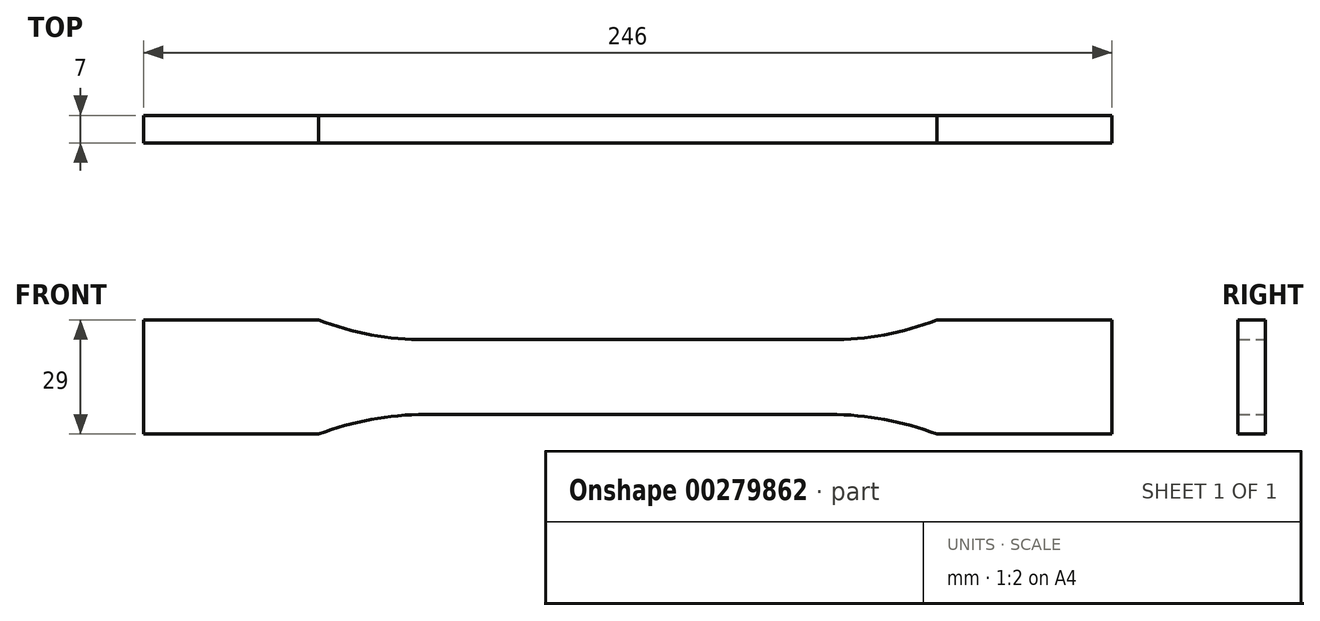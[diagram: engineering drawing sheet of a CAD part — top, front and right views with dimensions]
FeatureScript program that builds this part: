
annotation { "Feature Type Name" : "Feature", "Feature Type Description" : "" }
export const myFeature = defineFeature(function(context is Context, id is Id, definition is map)
    precondition{}
    {
        {
            var Q0;
            Q0=qCreatedBy(makeId("Front.planeOp"),FACE);
            var sketch = newSketch(context, id + "F0", { "sketchPlane" : qUnion([Q0])});
            skLineSegment(sketch, "E0", {"start": v(0, 9.5) * mm, "end": v(51.44, 9.5) * mm});
            skArc(sketch, "E1", {"start": v(51.44, 9.5) * mm, "mid": v(65.23, 10.76) * mm, "end": v(78.55, 14.5) * mm});
            skLineSegment(sketch, "E2", {"start": v(78.55, 14.5) * mm, "end": v(123, 14.5) * mm});
            skLineSegment(sketch, "E3.MirrorCS", {"start": v(78.55, -14.5) * mm, "end": v(123, -14.5) * mm});
            skLineSegment(sketch, "E4.MirrorCS", {"start": v(0, -9.5) * mm, "end": v(51.44, -9.5) * mm});
            skArc(sketch, "E5.MirrorCS", {"start": v(51.44, -9.5) * mm, "mid": v(65.23, -10.76) * mm, "end": v(78.55, -14.5) * mm});
            skArc(sketch, "E6.MirrorCS", {"start": v(-51.44, -9.5) * mm, "mid": v(-65.23, -10.76) * mm, "end": v(-78.55, -14.5) * mm});
            skLineSegment(sketch, "E7.MirrorCS", {"start": v(0, -9.5) * mm, "end": v(-51.44, -9.5) * mm});
            skArc(sketch, "E8.MirrorCS", {"start": v(-51.44, 9.5) * mm, "mid": v(-65.23, 10.76) * mm, "end": v(-78.55, 14.5) * mm});
            skLineSegment(sketch, "E9.MirrorCS", {"start": v(-78.55, 14.5) * mm, "end": v(-123, 14.5) * mm});
            skLineSegment(sketch, "E10.MirrorCS", {"start": v(-78.55, -14.5) * mm, "end": v(-123, -14.5) * mm});
            skLineSegment(sketch, "E11.MirrorCS", {"start": v(0, 9.5) * mm, "end": v(-51.44, 9.5) * mm});
            skLineSegment(sketch, "E12", {"start": v(-123, 14.5) * mm, "end": v(-123, -14.5) * mm});
            skLineSegment(sketch, "E13", {"start": v(123, 14.5) * mm, "end": v(123, -14.5) * mm});
            skSolve(sketch);
        }
        {
            var Q0;
            Q0=makeQuery(id+"F0.imprint","IMPRINT",FACE,{"disambiguationData":[TD([[makeQuery(id+"F0.imprint","IMPRINT",EDGE,{"derivedFrom":sQuery(id+"F0.wireOp",EDGE,"E4.MirrorCS")}),1.0]])]});
            extrude(context, id + "F1", {"entities" : qUnion([Q0]), "endBound" : BoundingType.SYMMETRIC, "depth" : 7 * mm});
        }
    });
